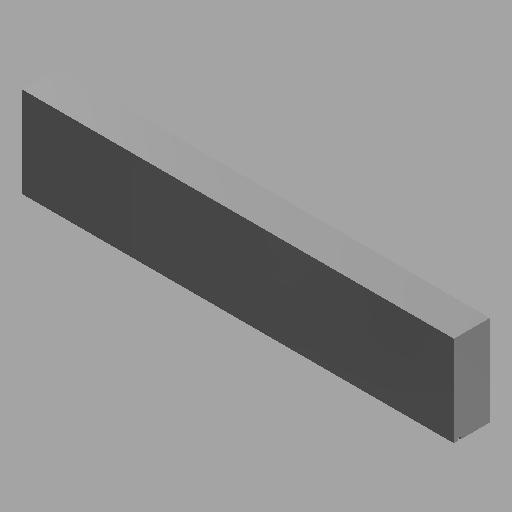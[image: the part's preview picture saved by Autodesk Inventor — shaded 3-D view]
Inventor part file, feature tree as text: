
AUTODESK INVENTOR PART (.ipt)
format: ipt  version: 2023 (Build 270158030, 158C)  size: 99,840 bytes
history: native  units: mm (DEFAULTED — no unit token found)
features: extrude x2, sketch x2
ambient origin geometry x8: Origin, YZ Plane, XZ Plane, XY Plane, X Axis, Y Axis, Z Axis, Center Point
bodies: Solid1 (feature_tree)
feature tree (4):
  extrude  "Extrusion1"  Depth=25.4mm TaperAngle=0.0deg
  extrude  "Extrusion2"  [1 undecoded]
  sketch  "Sketch1"  dims[d0=25.4mm d1=0.0mm d2=25.4mm d3=0.0mm]
  sketch  "Sketch2"
note: 1 required parameter value undecoded (feature->parameter linkage not recoverable at this tier; creation-order binding heuristic only, values carry confidence <= 0.55)
